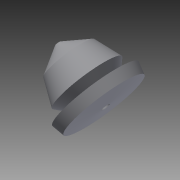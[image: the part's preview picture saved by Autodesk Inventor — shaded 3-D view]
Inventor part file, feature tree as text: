
AUTODESK INVENTOR PART (.ipt)
format: ipt  version: 2015 (Build 190159000, 159)  size: 103,424 bytes
history: native  units: in
note: dims shown in document units (in); Inventor stores cm internally (conversion verified against a paired STEP export)
features: revolve x1, sketch x1
ambient origin geometry x8: Origin, YZ Plane, XZ Plane, XY Plane, X Axis, Y Axis, Z Axis, Center Point
bodies: Solid1 (feature_tree)
feature tree (2):
  revolve  "Revolution1"  [1 undecoded]
  sketch  "Sketch1"  dims[d0=90.0deg]
note: 1 required parameter value undecoded (feature->parameter linkage not recoverable at this tier; creation-order binding heuristic only, values carry confidence <= 0.55)
